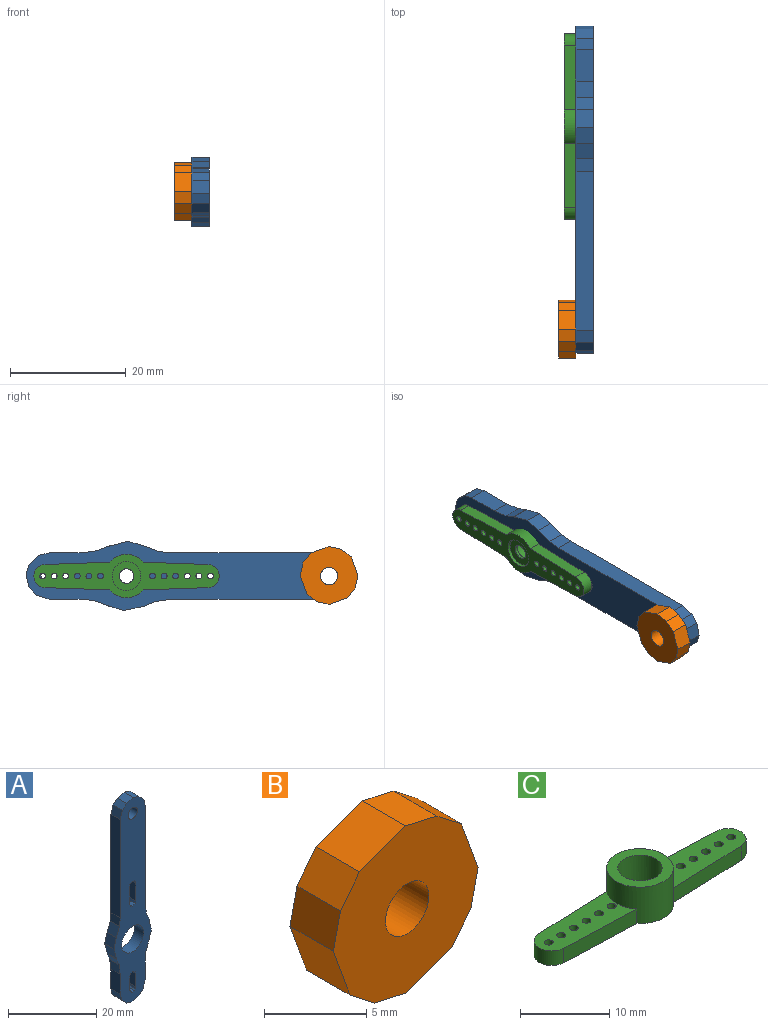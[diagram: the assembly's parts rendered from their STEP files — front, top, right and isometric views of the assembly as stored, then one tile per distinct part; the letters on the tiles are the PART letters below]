
ASSEMBLY  parts=3 mates=2
PART A: 58 faces, bbox 12x3x56.6 mm
  f0: plane 3x0.44mm, normal (0.29,0,0.96), area 1.4mm2, adj f1,f51,f55,f56
  f1: plane 3x0.42mm, normal (0.73,0,0.68), area 1.7mm2, adj f0,f2,f55,f56
  f2: plane 3x0.45mm, normal (0.97,0,0.23), area 1.4mm2, adj f1,f3,f55,f56
  f3: plane 3.7x3mm, normal (1,0,0), area 11.1mm2, adj f2,f4,f55,f56
  f4: plane 3x0.77mm, normal (0.91,0,-0.42), area 2.5mm2, adj f3,f5,f55,f56
  f5: plane 3x0.64mm, normal (0.34,0,-0.94), area 2mm2, adj f4,f6,f55,f56
  f6: plane 3x0.77mm, normal (-0.42,0,-0.91), area 2.5mm2, adj f5,f7,f55,f56
  f7: plane 3x0.64mm, normal (-0.94,0,-0.34), area 2mm2, adj f6,f8,f55,f56
  f8: plane 3.7x3mm, normal (-1,0,0), area 11.1mm2, adj f7,f9,f55,f56
  f9: plane 3x0.55mm, normal (-0.96,0,0.29), area 1.7mm2, adj f8,f10,f55,f56
  f10: plane 3x0.33mm, normal (-0.68,0,0.73), area 1.4mm2, adj f9,f51,f55,f56
  f11: plane 3x1.75mm, normal (-0.29,0,-0.96), area 5.5mm2, adj f12,f52,f55,f56
  f12: plane 3x2.25mm, normal (0.23,0,-0.97), area 6.9mm2, adj f11,f13,f55,f56
  f13: plane 3x1.33mm, normal (0.68,0,-0.73), area 5.5mm2, adj f12,f14,f55,f56
  f14: plane 3x2.21mm, normal (0.96,0,-0.29), area 6.9mm2, adj f13,f15,f55,f56
  f15: plane 5.53x3mm, normal (1,0,0), area 16.6mm2, adj f14,f16,f55,f56
  f16: plane 3x2.25mm, normal (0.99,0,-0.11), area 6.8mm2, adj f15,f17,f55,f56
  f17: plane 3x2.69mm, normal (0.94,0,-0.35), area 8.6mm2, adj f16,f18,f55,f56
  f18: plane 3x0.2mm, normal (-0.87,0,0.5), area 0.7mm2, adj f17,f19,f55,f56
  f19: plane 3x2.58mm, normal (0.95,0,-0.31), area 8.2mm2, adj f18,f20,f55,f56
  f20: plane 3.42x3mm, normal (0.98,0,0.21), area 10.5mm2, adj f19,f21,f55,f56
  f21: plane 3x2.09mm, normal (0.93,0,0.38), area 6.8mm2, adj f20,f22,f55,f56
  f22: plane 3x2.85mm, normal (0.99,0,0.14), area 8.6mm2, adj f21,f23,f55,f56
  f23: plane 27.35x3mm, normal (1,0,0), area 82.1mm2, adj f22,f24,f55,f56
  f24: plane 3x1.78mm, normal (0.97,0,0.23), area 5.5mm2, adj f23,f25,f55,f56
  f25: plane 3x1.68mm, normal (0.73,0,0.68), area 6.9mm2, adj f24,f26,f55,f56
  f26: plane 3x1.75mm, normal (0.29,0,0.96), area 5.5mm2, adj f25,f27,f55,f56
  f27: plane 3x2.25mm, normal (-0.23,0,0.97), area 6.9mm2, adj f26,f28,f55,f56
  f28: plane 3x1.33mm, normal (-0.68,0,0.73), area 5.5mm2, adj f27,f29,f55,f56
  f29: plane 3x2.21mm, normal (-0.96,0,0.29), area 6.9mm2, adj f28,f30,f55,f56
  f30: plane 27.35x3mm, normal (-1,0,0), area 82.1mm2, adj f29,f31,f55,f56
  f31: plane 3x2.25mm, normal (-0.99,0,0.11), area 6.8mm2, adj f30,f32,f55,f56
  f32: plane 3x2.69mm, normal (-0.94,0,0.35), area 8.6mm2, adj f31,f33,f55,f56
  f33: plane 3x2.69mm, normal (-0.96,0,0.27), area 8.4mm2, adj f32,f34,f55,f56
  f34: plane 3.34x3mm, normal (-0.97,0,-0.25), area 10.4mm2, adj f33,f35,f55,f56
  f35: plane 3x0.22mm, normal (0.87,0,0.5), area 0.8mm2, adj f34,f36,f55,f56
  f36: plane 3x2.09mm, normal (-0.93,0,-0.38), area 6.8mm2, adj f35,f37,f55,f56
  f37: plane 3x2.85mm, normal (-0.99,0,-0.14), area 8.6mm2, adj f36,f38,f55,f56
  f38: plane 5.53x3mm, normal (-1,0,0), area 16.6mm2, adj f37,f39,f55,f56
  f39: plane 3x1.78mm, normal (-0.97,0,-0.23), area 5.5mm2, adj f38,f52,f55,f56
  f40: plane 3x0.77mm, normal (-0.42,0,0.91), area 2.5mm2, adj f41,f53,f55,f56
  f41: plane 3x0.64mm, normal (0.34,0,0.94), area 2mm2, adj f40,f42,f55,f56
  f42: plane 3x0.77mm, normal (0.91,0,0.42), area 2.5mm2, adj f41,f43,f55,f56
  f43: plane 5x3mm, normal (1,0,0), area 15mm2, adj f42,f44,f55,f56
  f44: plane 3x0.45mm, normal (0.97,0,-0.23), area 1.4mm2, adj f43,f45,f55,f56
  f45: plane 3x0.42mm, normal (0.73,0,-0.68), area 1.7mm2, adj f44,f46,f55,f56
  f46: plane 3x0.44mm, normal (0.29,0,-0.96), area 1.4mm2, adj f45,f47,f55,f56
  f47: plane 3x0.56mm, normal (-0.23,0,-0.97), area 1.7mm2, adj f46,f48,f55,f56
  f48: plane 3x0.33mm, normal (-0.68,0,-0.73), area 1.4mm2, adj f47,f49,f55,f56
  f49: plane 3x0.55mm, normal (-0.96,0,-0.29), area 1.7mm2, adj f48,f50,f55,f56
  f50: plane 5x3mm, normal (-1,0,0), area 15mm2, adj f49,f53,f55,f56
  f51: plane 3x0.56mm, normal (-0.23,0,0.97), area 1.7mm2, adj f0,f10,f55,f56
  f52: plane 3x1.68mm, normal (-0.73,0,-0.68), area 6.9mm2, adj f11,f39,f55,f56
  f53: plane 3x0.64mm, normal (-0.94,0,0.34), area 2mm2, adj f40,f50,f55,f56
  f54: cylinder r=3.55mm len=7.1mm, axis (0,1,0), area 66.9mm2, adj f55,f56
  f55: plane 56.56x11.97mm, normal (0,-1,0), area 394.4mm2, adj f0,f1,f2,f3,f4,f5,f6,f7
  f56: plane 56.56x11.97mm, normal (0,1,0), area 394.4mm2, adj f0,f1,f2,f3,f4,f5,f6,f7
  f57: cylinder r=1.5mm len=3mm, axis (0,-1,0), area 28.3mm2, adj f55,f56
PART B: 15 faces, bbox 10x3x10 mm
  f0: plane 3.2x3mm, normal (-0.94,0,-0.34), area 10.2mm2, adj f1,f11,f13,f14
  f1: plane 3x1.69mm, normal (-0.62,0,-0.79), area 6.4mm2, adj f0,f2,f13,f14
  f2: plane 3x2.16mm, normal (-0.22,0,-0.98), area 6.6mm2, adj f1,f3,f13,f14
  f3: plane 3.2x3mm, normal (0.34,0,-0.94), area 10.2mm2, adj f2,f4,f13,f14
  f4: plane 3x1.69mm, normal (0.79,0,-0.62), area 6.4mm2, adj f3,f5,f13,f14
  f5: plane 3x2.16mm, normal (0.98,0,-0.22), area 6.6mm2, adj f4,f6,f13,f14
  f6: plane 3.2x3mm, normal (0.94,0,0.34), area 10.2mm2, adj f5,f7,f13,f14
  f7: plane 3x1.69mm, normal (0.62,0,0.79), area 6.4mm2, adj f6,f8,f13,f14
  f8: plane 3x2.16mm, normal (0.22,0,0.98), area 6.6mm2, adj f7,f9,f13,f14
  f9: plane 3.2x3mm, normal (-0.34,0,0.94), area 10.2mm2, adj f8,f10,f13,f14
  f10: plane 3x1.69mm, normal (-0.79,0,0.62), area 6.4mm2, adj f9,f11,f13,f14
  f11: plane 3x2.16mm, normal (-0.98,0,0.22), area 6.6mm2, adj f0,f10,f13,f14
  f12: cylinder r=1.5mm len=3mm, axis (0,1,0), area 28.3mm2, adj f13,f14
  f13: plane 10x10mm, normal (0,-1,0), area 67.4mm2, adj f0,f1,f2,f3,f4,f5,f6,f7
  f14: plane 10x10mm, normal (0,1,0), area 67.4mm2, adj f0,f1,f2,f3,f4,f5,f6,f7
PART C: 28 faces, bbox 32x7.5x5 mm
  f0: cylinder r=2.5mm len=5mm, axis (0,0,1), area 62.8mm2, adj f11,f24
  f1: plane 13.11x4.79mm, normal (0,0,1), area 47.6mm2, adj f7,f8,f9,f10,f17,f18,f19,f20
  f2: plane 32x7.5mm, normal (0,0,-1), area 119.7mm2, adj f3,f4,f5,f7,f8,f9,f10,f12
  f3: plane 11.19x2mm, normal (0.04,-1,0), area 22.4mm2, adj f2,f4,f6,f7
  f4: cylinder r=2mm len=4mm, axis (0,0,-1), area 12.3mm2, adj f2,f3,f5,f6
  f5: plane 11.19x2mm, normal (0.04,1,0), area 22.4mm2, adj f2,f4,f6,f7
  f6: plane 13.11x4.79mm, normal (0,0,1), area 47.6mm2, adj f3,f4,f5,f7,f12,f13,f14,f15
  f7: cylinder r=3.75mm len=7.5mm, axis (0,0,1), area 97mm2, adj f1,f2,f3,f5,f6,f9,f10,f11
  f8: cylinder r=2mm len=4mm, axis (0,0,-1), area 12.3mm2, adj f1,f2,f9,f10
  f9: plane 11.19x2mm, normal (-0.04,-1,0), area 22.4mm2, adj f1,f2,f7,f8
  f10: plane 11.19x2mm, normal (-0.04,1,0), area 22.4mm2, adj f1,f2,f7,f8
  f11: plane 7.5x7.5mm, normal (0,0,1), area 24.5mm2, adj f0,f7
  f12: cylinder r=0.5mm len=2mm, axis (0,0,-1), area 6.3mm2, adj f2,f6
  f13: cylinder r=0.5mm len=2mm, axis (0,0,-1), area 6.3mm2, adj f2,f6
  f14: cylinder r=0.5mm len=2mm, axis (0,0,-1), area 6.3mm2, adj f2,f6
  f15: cylinder r=0.5mm len=2mm, axis (0,0,-1), area 6.3mm2, adj f2,f6
  f16: cylinder r=0.5mm len=2mm, axis (0,0,-1), area 6.3mm2, adj f2,f6
  f17: cylinder r=0.5mm len=2mm, axis (0,0,-1), area 6.3mm2, adj f1,f2
  f18: cylinder r=0.5mm len=2mm, axis (0,0,-1), area 6.3mm2, adj f1,f2
  f19: cylinder r=0.5mm len=2mm, axis (0,0,-1), area 6.3mm2, adj f1,f2
  f20: cylinder r=0.5mm len=2mm, axis (0,0,-1), area 6.3mm2, adj f1,f2
  f21: cylinder r=0.5mm len=2mm, axis (0,0,-1), area 6.3mm2, adj f1,f2
  f22: cylinder r=0.5mm len=2mm, axis (0,0,-1), area 6.3mm2, adj f1,f2
  f23: cylinder r=0.5mm len=2mm, axis (0,0,-1), area 6.3mm2, adj f2,f6
  f24: plane 5x5mm, normal (0,0,1), area 14.7mm2, adj f0,f27
  f25: cylinder r=2.5mm len=5mm, axis (0,0,-1), area 7.9mm2, adj f2,f26
  f26: plane 5x5mm, normal (0,0,-1), area 14.7mm2, adj f25,f27
  f27: cylinder r=1.25mm len=2.5mm, axis (0,0,-1), area 3.9mm2, adj f24,f26
PLACE A rot(axis=(0.58,0.58,-0.58),120deg) t=(0,-75.9,-133)mm
PLACE B rot(axis=(0.58,0.58,-0.58),120deg) t=(-3,-68.33,-125.05)mm
PLACE C rot(axis=(-0.58,0.58,-0.58),120deg) t=(-5,0,0)mm
MATE fastened C.f0 <-> A.f54  axis (1,0,0) through (-3,0,0)mm
MATE fastened B.f12 <-> A.f57  axis (1,0,0) through (-3,-35,0)mm
